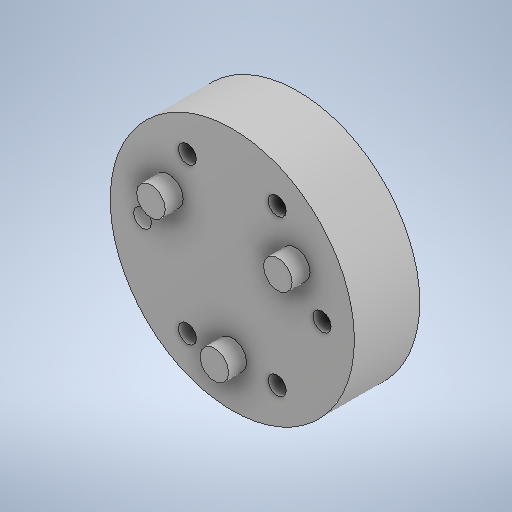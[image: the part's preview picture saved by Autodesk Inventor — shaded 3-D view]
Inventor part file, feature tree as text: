
AUTODESK INVENTOR PART (.ipt)
format: ipt  version: 2025.2 (Build 292293000, 293)  size: 262,656 bytes
history: native  units: in
note: dims shown in document units (in); Inventor stores cm internally (conversion verified against a paired STEP export)
features: extrude x2, sketch x2, plane x1
ambient origin geometry x8: Origin, YZ Plane, XZ Plane, XY Plane, X Axis, Y Axis, Z Axis, Center Point
bodies: Solid1 (feature_tree), Body1 (feature_tree)
feature tree (5):
  extrude  "Extrusion1"  [1 undecoded]
  plane  "Work Plane1"
  extrude  "Extrusion2"  [1 undecoded]
  sketch  "Sketch1"  dims[d0=0.0in d1=0.0in d2=-0.4567in]
  sketch  "Sketch2"  dims[d3=0.0in d4=0.0in]
note: 2 required parameter values undecoded (feature->parameter linkage not recoverable at this tier; creation-order binding heuristic only, values carry confidence <= 0.55)
